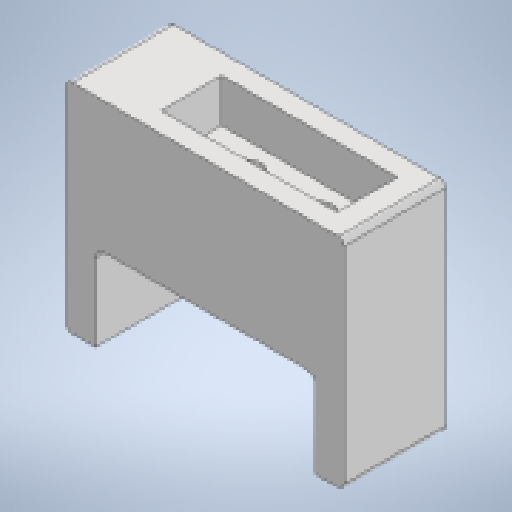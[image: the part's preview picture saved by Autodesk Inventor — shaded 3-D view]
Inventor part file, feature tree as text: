
AUTODESK INVENTOR PART (.ipt)
format: ipt  version: 2023 (Build 270158000, 158)  size: 197,120 bytes
history: native  units: in
note: dims shown in document units (in); Inventor stores cm internally (conversion verified against a paired STEP export)
features: extrude x6, sketch x5, fillet x2
ambient origin geometry x8: Origin, YZ Plane, XZ Plane, XY Plane, X Axis, Y Axis, Z Axis, Center Point
bodies: Solid1 (feature_tree)
feature tree (13):
  sketch  "Sketch1"  dims[d0=0.7874in d1=2.3622in]
  extrude  "Extrusion1"  Depth=0.7874in
  extrude  "Extrusion2"  Depth=0.0197in
  extrude  "Extrusion3"  Depth=0.0197in
  extrude  "Extrusion4"  Depth=1.811in
  extrude  "Extrusion5"  Depth=1.378in
  extrude  "Extrusion6"  Depth=0.3937in TaperAngle=0.0deg
  fillet  "Fillet1"  Radius=1.3937in
  fillet  "Fillet2"  Radius=0.3937in
  sketch  "Sketch2"  dims[d2=0.0197in d3=0.0197in]
  sketch  "Sketch3"  dims[d4=0.0197in d5=0.0197in]
  sketch  "Sketch4"  dims[d6=0.1417in d7=1.811in]
  sketch  "Sketch5"  dims[d9=4.1811in d10=1.378in d11=0.3937in d12=0.0in d13=1.3937in d14=0.0in d15=0.3937in d16=0.1969in d17=0.0in d18=0.0in d19=0.3937in d20=1.1969in d21=0.0in d22=0.0in d23=3.0in d24=0.125in d25=0.7874in d26=1.1811in d27=0.3937in d28=0.0in d29=0.2362in d30=0.9843in d31=0.3937in d32=0.0in d34=0.4724in d35=0.3937in d36=0.0in d37=0.0787in d38=0.0787in d43=0.3937in]
